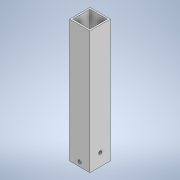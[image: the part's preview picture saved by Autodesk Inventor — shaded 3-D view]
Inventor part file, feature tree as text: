
AUTODESK INVENTOR PART (.ipt)
format: ipt  version: 2022 (Build 260153000, 153)  size: 117,760 bytes
history: native  units: mm
features: extrude x3, sketch x3
ambient origin geometry x8: Origin, YZ Plane, XZ Plane, XY Plane, X Axis, Y Axis, Z Axis, Center Point
bodies: Solid1 (feature_tree)
feature tree (6):
  extrude  "Extrusion1"  Depth=25.4mm
  extrude  "Extrusion2"  Depth=152.4mm TaperAngle=0.0deg
  extrude  "Extrusion3"  Depth=152.4mm TaperAngle=0.0deg
  sketch  "Sketch1"  dims[d0=25.4mm d1=25.4mm]
  sketch  "Sketch2"  dims[d2=2.0mm d3=152.4mm d4=0.0mm]
  sketch  "Sketch3"  dims[d6=4.0mm d7=152.4mm d8=0.0mm d10=4.0mm d11=0.0mm d12=0.0mm]
